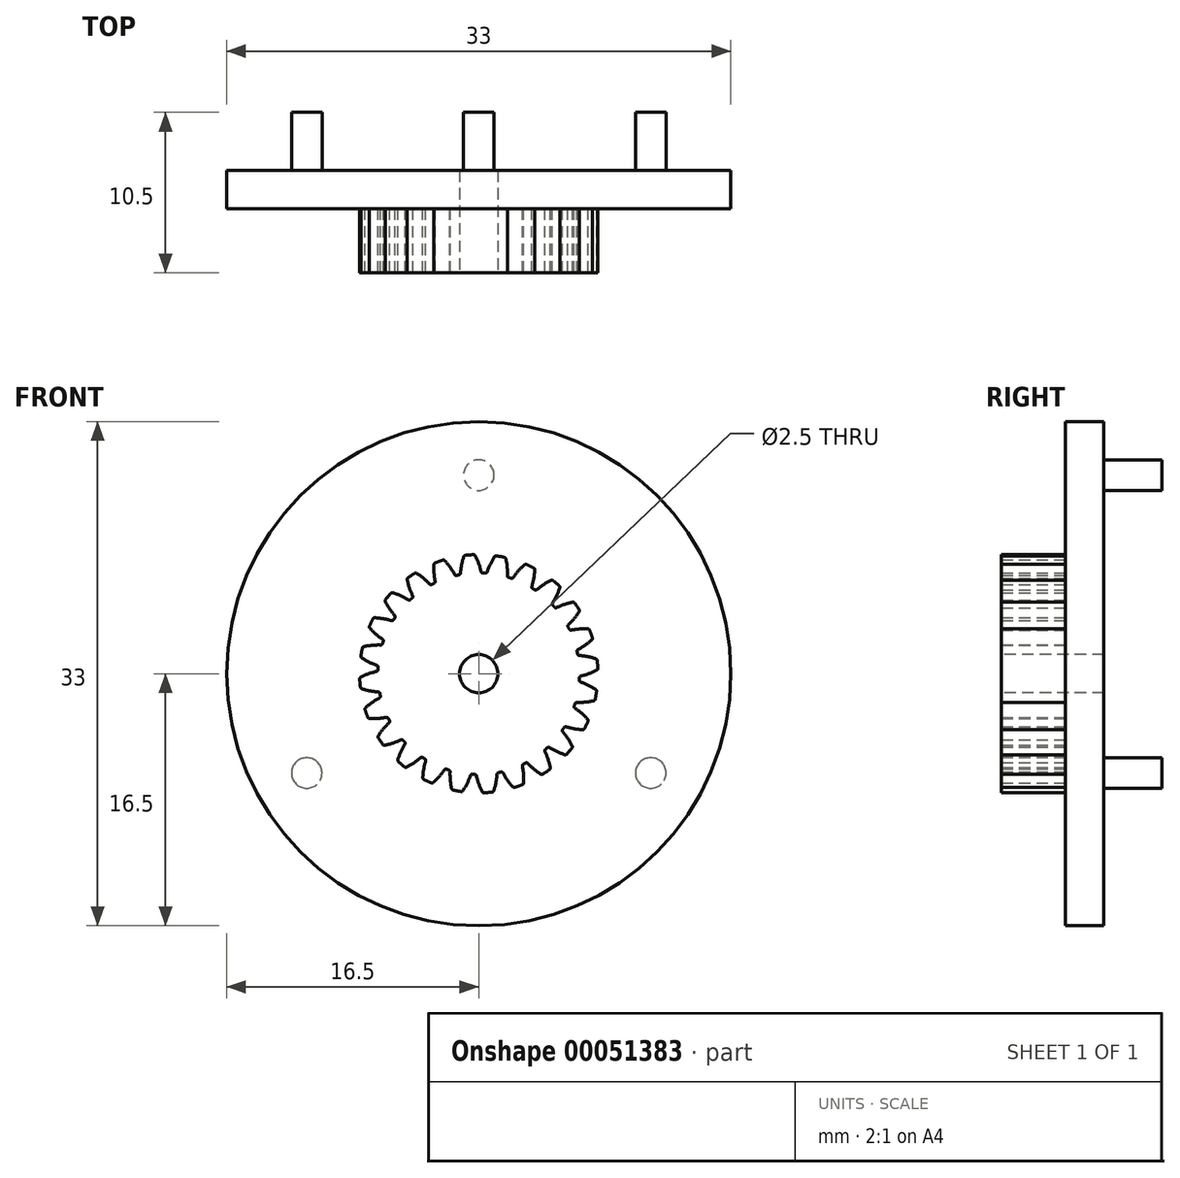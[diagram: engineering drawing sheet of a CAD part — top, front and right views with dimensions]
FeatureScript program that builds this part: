
annotation { "Feature Type Name" : "Feature", "Feature Type Description" : "" }
export const myFeature = defineFeature(function(context is Context, id is Id, definition is map)
    precondition{}
    {
        {
            var Q0;
            Q0=qCreatedBy(makeId("Front.planeOp"),FACE);
            var sketch = newSketch(context, id + "F0", { "sketchPlane" : qUnion([Q0])});
            skCircle(sketch, "E0", {"center": v(0, 0) * mm, "radius": 7.2 * mm, "construction": true});
            skCircle(sketch, "E1", {"center": v(0, 0) * mm, "radius": 6.6 * mm, "construction": true});
            skCircle(sketch, "E2", {"center": v(0, 0) * mm, "radius": 7.8 * mm, "construction": true});
            skLineSegment(sketch, "E3", {"start": v(0, 0) * mm, "end": v(0, 7.77) * mm, "construction": true});
            skPoint(sketch, "E4", {"position": v(0, 7.2) * mm});
            skLineSegment(sketch, "E5", {"start": v(0, 7.2) * mm, "end": v(-7.8, 7.2) * mm, "construction": true});
            skCircle(sketch, "E6.cCircle", {"center": v(0, 0) * mm, "radius": 7.77 * mm, "construction": true});
            skLineSegment(sketch, "E6.0", {"start": v(-0.61, 7.77) * mm, "end": v(0.61, 7.77) * mm, "construction": true});
            skLineSegment(sketch, "E6.1", {"start": v(0.61, 7.77) * mm, "end": v(1.82, 7.58) * mm, "construction": true});
            skLineSegment(sketch, "E6.2", {"start": v(1.82, 7.58) * mm, "end": v(2.98, 7.2) * mm, "construction": true});
            skLineSegment(sketch, "E6.3", {"start": v(2.98, 7.2) * mm, "end": v(4.07, 6.65) * mm, "construction": true});
            skLineSegment(sketch, "E6.4", {"start": v(4.07, 6.65) * mm, "end": v(5.06, 5.93) * mm, "construction": true});
            skLineSegment(sketch, "E6.5", {"start": v(5.06, 5.93) * mm, "end": v(5.93, 5.06) * mm, "construction": true});
            skLineSegment(sketch, "E6.6", {"start": v(5.93, 5.06) * mm, "end": v(6.65, 4.07) * mm, "construction": true});
            skLineSegment(sketch, "E6.7", {"start": v(6.65, 4.07) * mm, "end": v(7.2, 2.98) * mm, "construction": true});
            skLineSegment(sketch, "E6.8", {"start": v(7.2, 2.98) * mm, "end": v(7.58, 1.82) * mm, "construction": true});
            skLineSegment(sketch, "E6.9", {"start": v(7.58, 1.82) * mm, "end": v(7.77, 0.61) * mm, "construction": true});
            skLineSegment(sketch, "E6.10", {"start": v(7.77, 0.61) * mm, "end": v(7.77, -0.61) * mm, "construction": true});
            skLineSegment(sketch, "E6.11", {"start": v(7.77, -0.61) * mm, "end": v(7.58, -1.82) * mm, "construction": true});
            skLineSegment(sketch, "E6.12", {"start": v(7.58, -1.82) * mm, "end": v(7.2, -2.98) * mm, "construction": true});
            skLineSegment(sketch, "E6.13", {"start": v(7.2, -2.98) * mm, "end": v(6.65, -4.07) * mm, "construction": true});
            skLineSegment(sketch, "E6.14", {"start": v(6.65, -4.07) * mm, "end": v(5.93, -5.06) * mm, "construction": true});
            skLineSegment(sketch, "E6.15", {"start": v(5.93, -5.06) * mm, "end": v(5.06, -5.93) * mm, "construction": true});
            skLineSegment(sketch, "E6.16", {"start": v(5.06, -5.93) * mm, "end": v(4.07, -6.65) * mm, "construction": true});
            skLineSegment(sketch, "E6.17", {"start": v(4.07, -6.65) * mm, "end": v(2.98, -7.2) * mm, "construction": true});
            skLineSegment(sketch, "E6.18", {"start": v(2.98, -7.2) * mm, "end": v(1.82, -7.58) * mm, "construction": true});
            skLineSegment(sketch, "E6.19", {"start": v(1.82, -7.58) * mm, "end": v(0.61, -7.77) * mm, "construction": true});
            skLineSegment(sketch, "E6.20", {"start": v(0.61, -7.77) * mm, "end": v(-0.61, -7.77) * mm, "construction": true});
            skLineSegment(sketch, "E6.21", {"start": v(-0.61, -7.77) * mm, "end": v(-1.82, -7.58) * mm, "construction": true});
            skLineSegment(sketch, "E6.22", {"start": v(-1.82, -7.58) * mm, "end": v(-2.98, -7.2) * mm, "construction": true});
            skLineSegment(sketch, "E6.23", {"start": v(-2.98, -7.2) * mm, "end": v(-4.07, -6.65) * mm, "construction": true});
            skLineSegment(sketch, "E6.24", {"start": v(-4.07, -6.65) * mm, "end": v(-5.06, -5.93) * mm, "construction": true});
            skLineSegment(sketch, "E6.25", {"start": v(-5.06, -5.93) * mm, "end": v(-5.93, -5.06) * mm, "construction": true});
            skLineSegment(sketch, "E6.26", {"start": v(-5.93, -5.06) * mm, "end": v(-6.65, -4.07) * mm, "construction": true});
            skLineSegment(sketch, "E6.27", {"start": v(-6.65, -4.07) * mm, "end": v(-7.2, -2.98) * mm, "construction": true});
            skLineSegment(sketch, "E6.28", {"start": v(-7.2, -2.98) * mm, "end": v(-7.58, -1.82) * mm, "construction": true});
            skLineSegment(sketch, "E6.29", {"start": v(-7.58, -1.82) * mm, "end": v(-7.77, -0.61) * mm, "construction": true});
            skLineSegment(sketch, "E6.30", {"start": v(-7.77, -0.61) * mm, "end": v(-7.77, 0.61) * mm, "construction": true});
            skLineSegment(sketch, "E6.31", {"start": v(-7.77, 0.61) * mm, "end": v(-7.58, 1.82) * mm, "construction": true});
            skLineSegment(sketch, "E6.32", {"start": v(-7.58, 1.82) * mm, "end": v(-7.2, 2.98) * mm, "construction": true});
            skLineSegment(sketch, "E6.33", {"start": v(-7.2, 2.98) * mm, "end": v(-6.65, 4.07) * mm, "construction": true});
            skLineSegment(sketch, "E6.34", {"start": v(-6.65, 4.07) * mm, "end": v(-5.93, 5.06) * mm, "construction": true});
            skLineSegment(sketch, "E6.35", {"start": v(-5.93, 5.06) * mm, "end": v(-5.06, 5.93) * mm, "construction": true});
            skLineSegment(sketch, "E6.36", {"start": v(-5.06, 5.93) * mm, "end": v(-4.07, 6.65) * mm, "construction": true});
            skLineSegment(sketch, "E6.37", {"start": v(-4.07, 6.65) * mm, "end": v(-2.98, 7.2) * mm, "construction": true});
            skLineSegment(sketch, "E6.38", {"start": v(-2.98, 7.2) * mm, "end": v(-1.82, 7.58) * mm, "construction": true});
            skLineSegment(sketch, "E6.39", {"start": v(-1.82, 7.58) * mm, "end": v(-0.61, 7.77) * mm, "construction": true});
            skPoint(sketch, "E6.0.midPoint", {"position": v(0, 7.77) * mm});
            skLineSegment(sketch, "E7.0", {"start": v(0, 7.77) * mm, "end": v(1.22, 7.68) * mm, "construction": true});
            skLineSegment(sketch, "E7.1", {"start": v(1.22, 7.68) * mm, "end": v(2.4, 7.4) * mm, "construction": true});
            skLineSegment(sketch, "E7.2", {"start": v(2.4, 7.4) * mm, "end": v(3.53, 6.93) * mm, "construction": true});
            skLineSegment(sketch, "E7.3", {"start": v(3.53, 6.93) * mm, "end": v(4.57, 6.29) * mm, "construction": true});
            skLineSegment(sketch, "E7.4", {"start": v(4.57, 6.29) * mm, "end": v(5.5, 5.5) * mm, "construction": true});
            skLineSegment(sketch, "E7.5", {"start": v(5.5, 5.5) * mm, "end": v(6.29, 4.57) * mm, "construction": true});
            skLineSegment(sketch, "E7.6", {"start": v(6.29, 4.57) * mm, "end": v(6.93, 3.53) * mm, "construction": true});
            skLineSegment(sketch, "E7.7", {"start": v(6.93, 3.53) * mm, "end": v(7.4, 2.4) * mm, "construction": true});
            skLineSegment(sketch, "E7.8", {"start": v(7.4, 2.4) * mm, "end": v(7.68, 1.22) * mm, "construction": true});
            skLineSegment(sketch, "E7.9", {"start": v(7.68, 1.22) * mm, "end": v(7.77, 0) * mm, "construction": true});
            skLineSegment(sketch, "E7.10", {"start": v(7.77, 0) * mm, "end": v(7.68, -1.22) * mm, "construction": true});
            skLineSegment(sketch, "E7.11", {"start": v(7.68, -1.22) * mm, "end": v(7.4, -2.4) * mm, "construction": true});
            skLineSegment(sketch, "E7.12", {"start": v(7.4, -2.4) * mm, "end": v(6.93, -3.53) * mm, "construction": true});
            skLineSegment(sketch, "E7.13", {"start": v(6.93, -3.53) * mm, "end": v(6.29, -4.57) * mm, "construction": true});
            skLineSegment(sketch, "E7.14", {"start": v(6.29, -4.57) * mm, "end": v(5.5, -5.5) * mm, "construction": true});
            skLineSegment(sketch, "E7.15", {"start": v(5.5, -5.5) * mm, "end": v(4.57, -6.29) * mm, "construction": true});
            skLineSegment(sketch, "E7.16", {"start": v(4.57, -6.29) * mm, "end": v(3.53, -6.93) * mm, "construction": true});
            skLineSegment(sketch, "E7.17", {"start": v(3.53, -6.93) * mm, "end": v(2.4, -7.4) * mm, "construction": true});
            skLineSegment(sketch, "E7.18", {"start": v(2.4, -7.4) * mm, "end": v(1.22, -7.68) * mm, "construction": true});
            skLineSegment(sketch, "E7.19", {"start": v(1.22, -7.68) * mm, "end": v(0, -7.77) * mm, "construction": true});
            skLineSegment(sketch, "E7.20", {"start": v(0, -7.77) * mm, "end": v(-1.22, -7.68) * mm, "construction": true});
            skLineSegment(sketch, "E7.21", {"start": v(-1.22, -7.68) * mm, "end": v(-2.4, -7.4) * mm, "construction": true});
            skLineSegment(sketch, "E7.22", {"start": v(-2.4, -7.4) * mm, "end": v(-3.53, -6.93) * mm, "construction": true});
            skLineSegment(sketch, "E7.23", {"start": v(-3.53, -6.93) * mm, "end": v(-4.57, -6.29) * mm, "construction": true});
            skLineSegment(sketch, "E7.24", {"start": v(-4.57, -6.29) * mm, "end": v(-5.5, -5.5) * mm, "construction": true});
            skLineSegment(sketch, "E7.25", {"start": v(-5.5, -5.5) * mm, "end": v(-6.29, -4.57) * mm, "construction": true});
            skLineSegment(sketch, "E7.26", {"start": v(-6.29, -4.57) * mm, "end": v(-6.93, -3.53) * mm, "construction": true});
            skLineSegment(sketch, "E7.27", {"start": v(-6.93, -3.53) * mm, "end": v(-7.4, -2.4) * mm, "construction": true});
            skLineSegment(sketch, "E7.28", {"start": v(-7.4, -2.4) * mm, "end": v(-7.68, -1.22) * mm, "construction": true});
            skLineSegment(sketch, "E7.29", {"start": v(-7.68, -1.22) * mm, "end": v(-7.77, 0) * mm, "construction": true});
            skLineSegment(sketch, "E7.30", {"start": v(-7.77, 0) * mm, "end": v(-7.68, 1.22) * mm, "construction": true});
            skLineSegment(sketch, "E7.31", {"start": v(-7.68, 1.22) * mm, "end": v(-7.4, 2.4) * mm, "construction": true});
            skLineSegment(sketch, "E7.32", {"start": v(-7.4, 2.4) * mm, "end": v(-6.93, 3.53) * mm, "construction": true});
            skLineSegment(sketch, "E7.33", {"start": v(-6.93, 3.53) * mm, "end": v(-6.29, 4.57) * mm, "construction": true});
            skLineSegment(sketch, "E7.34", {"start": v(-6.29, 4.57) * mm, "end": v(-5.5, 5.5) * mm, "construction": true});
            skLineSegment(sketch, "E7.35", {"start": v(-5.5, 5.5) * mm, "end": v(-4.57, 6.29) * mm, "construction": true});
            skLineSegment(sketch, "E7.36", {"start": v(-4.57, 6.29) * mm, "end": v(-3.53, 6.93) * mm, "construction": true});
            skLineSegment(sketch, "E7.37", {"start": v(-3.53, 6.93) * mm, "end": v(-2.4, 7.4) * mm, "construction": true});
            skLineSegment(sketch, "E7.38", {"start": v(-2.4, 7.4) * mm, "end": v(-1.22, 7.68) * mm, "construction": true});
            skLineSegment(sketch, "E7.39", {"start": v(-1.22, 7.68) * mm, "end": v(0, 7.77) * mm, "construction": true});
            skLineSegment(sketch, "E8", {"start": v(0, 0) * mm, "end": v(-0.61, 7.77) * mm, "construction": true});
            skLineSegment(sketch, "E9", {"start": v(0, 7.2) * mm, "end": v(-7.35, 4.52) * mm, "construction": true});
            skCircle(sketch, "E10", {"center": v(0, 7.2) * mm, "radius": 4.32 * mm, "construction": true});
            skPoint(sketch, "E11", {"position": v(-4.06, 5.72) * mm});
            skCircle(sketch, "E12", {"center": v(-4.06, 5.72) * mm, "radius": 4.32 * mm, "construction": true});
            skArc(sketch, "E13", {"start": v(-0.23, 7.73) * mm, "mid": v(0, 7.22) * mm, "end": v(0.15, 6.69) * mm});
            skArc(sketch, "E14.MirrorCS", {"start": v(-0.98, 7.67) * mm, "mid": v(-1.12, 7.13) * mm, "end": v(-1.2, 6.58) * mm});
            skArc(sketch, "E15", {"start": v(-0.88, 7.75) * mm, "mid": v(-0.61, 7.78) * mm, "end": v(-0.34, 7.8) * mm});
            skArc(sketch, "E16", {"start": v(-1.3, 6.47) * mm, "mid": v(0.52, -6.58) * mm, "end": v(0.26, 6.6) * mm});
            skPoint(sketch, "E17.visualSharp", {"position": v(-1.2, 6.49) * mm});
            skArc(sketch, "E17.filletArc", {"start": v(-1.3, 6.47) * mm, "mid": v(-1.23, 6.51) * mm, "end": v(-1.2, 6.58) * mm});
            skPoint(sketch, "E18.visualSharp", {"position": v(0.17, 6.6) * mm});
            skArc(sketch, "E18.filletArc", {"start": v(0.15, 6.69) * mm, "mid": v(0.2, 6.62) * mm, "end": v(0.26, 6.6) * mm});
            skPoint(sketch, "E19.visualSharp", {"position": v(-0.95, 7.74) * mm});
            skArc(sketch, "E19.filletArc", {"start": v(-0.88, 7.75) * mm, "mid": v(-0.94, 7.72) * mm, "end": v(-0.98, 7.67) * mm});
            skPoint(sketch, "E20.visualSharp", {"position": v(-0.27, 7.8) * mm});
            skArc(sketch, "E20.filletArc", {"start": v(-0.23, 7.73) * mm, "mid": v(-0.28, 7.78) * mm, "end": v(-0.34, 7.8) * mm});
            skLineSegment(sketch, "E21", {"start": v(0, 0) * mm, "end": v(-1.62, 8.11) * mm, "construction": true});
            skPoint(sketch, "E22.1.0", {"position": v(-1.54, 6.42) * mm});
            skPoint(sketch, "E22.1.1", {"position": v(-1.86, 6.95) * mm});
            skArc(sketch, "E22.1.2", {"start": v(-2.23, 7.4) * mm, "mid": v(-1.88, 6.97) * mm, "end": v(-1.58, 6.5) * mm});
            skArc(sketch, "E22.1.3", {"start": v(-2.85, 7.26) * mm, "mid": v(-2.6, 7.35) * mm, "end": v(-2.35, 7.44) * mm});
            skPoint(sketch, "E22.1.4", {"position": v(-2.28, 7.46) * mm});
            skPoint(sketch, "E22.1.5", {"position": v(-2.84, 5.96) * mm});
            skArc(sketch, "E22.1.6", {"start": v(-2.93, 7.15) * mm, "mid": v(-2.93, 6.6) * mm, "end": v(-2.86, 6.05) * mm});
            skPoint(sketch, "E22.1.7", {"position": v(-2.92, 7.23) * mm});
            skArc(sketch, "E22.1.8", {"start": v(-1.58, 6.5) * mm, "mid": v(-1.53, 6.45) * mm, "end": v(-1.45, 6.44) * mm});
            skArc(sketch, "E22.1.9", {"start": v(-2.85, 7.26) * mm, "mid": v(-2.9, 7.22) * mm, "end": v(-2.93, 7.15) * mm});
            skArc(sketch, "E22.1.10", {"start": v(-2.92, 5.92) * mm, "mid": v(-2.87, 5.97) * mm, "end": v(-2.86, 6.05) * mm});
            skArc(sketch, "E22.1.11", {"start": v(-2.23, 7.4) * mm, "mid": v(-2.28, 7.44) * mm, "end": v(-2.35, 7.44) * mm});
            skPoint(sketch, "E22.2.0", {"position": v(-3.15, 5.8) * mm});
            skPoint(sketch, "E22.2.1", {"position": v(-3.6, 6.24) * mm});
            skArc(sketch, "E22.2.2", {"start": v(-4.07, 6.58) * mm, "mid": v(-3.62, 6.25) * mm, "end": v(-3.21, 5.87) * mm});
            skArc(sketch, "E22.2.3", {"start": v(-4.64, 6.27) * mm, "mid": v(-4.42, 6.43) * mm, "end": v(-4.2, 6.58) * mm});
            skPoint(sketch, "E22.2.4", {"position": v(-4.13, 6.62) * mm});
            skPoint(sketch, "E22.2.5", {"position": v(-4.28, 5.02) * mm});
            skArc(sketch, "E22.2.6", {"start": v(-4.68, 6.15) * mm, "mid": v(-4.54, 5.62) * mm, "end": v(-4.33, 5.1) * mm});
            skPoint(sketch, "E22.2.7", {"position": v(-4.7, 6.23) * mm});
            skArc(sketch, "E22.2.8", {"start": v(-3.21, 5.87) * mm, "mid": v(-3.15, 5.83) * mm, "end": v(-3.07, 5.84) * mm});
            skArc(sketch, "E22.2.9", {"start": v(-4.64, 6.27) * mm, "mid": v(-4.68, 6.22) * mm, "end": v(-4.68, 6.15) * mm});
            skArc(sketch, "E22.2.10", {"start": v(-4.35, 4.96) * mm, "mid": v(-4.32, 5.03) * mm, "end": v(-4.33, 5.1) * mm});
            skArc(sketch, "E22.2.11", {"start": v(-4.07, 6.58) * mm, "mid": v(-4.13, 6.6) * mm, "end": v(-4.2, 6.58) * mm});
            skPoint(sketch, "E22.3.0", {"position": v(-4.54, 4.79) * mm});
            skPoint(sketch, "E22.3.1", {"position": v(-5.1, 5.1) * mm});
            skArc(sketch, "E22.3.2", {"start": v(-5.63, 5.3) * mm, "mid": v(-5.11, 5.1) * mm, "end": v(-4.62, 4.84) * mm});
            skArc(sketch, "E22.3.3", {"start": v(-6.1, 4.86) * mm, "mid": v(-5.93, 5.07) * mm, "end": v(-5.75, 5.27) * mm});
            skPoint(sketch, "E22.3.4", {"position": v(-5.7, 5.32) * mm});
            skPoint(sketch, "E22.3.5", {"position": v(-5.44, 3.74) * mm});
            skArc(sketch, "E22.3.6", {"start": v(-6.12, 4.73) * mm, "mid": v(-5.84, 4.25) * mm, "end": v(-5.5, 3.8) * mm});
            skPoint(sketch, "E22.3.7", {"position": v(-6.15, 4.8) * mm});
            skArc(sketch, "E22.3.8", {"start": v(-4.62, 4.84) * mm, "mid": v(-4.55, 4.82) * mm, "end": v(-4.48, 4.85) * mm});
            skArc(sketch, "E22.3.9", {"start": v(-6.1, 4.86) * mm, "mid": v(-6.13, 4.8) * mm, "end": v(-6.12, 4.73) * mm});
            skArc(sketch, "E22.3.10", {"start": v(-5.5, 3.66) * mm, "mid": v(-5.47, 3.74) * mm, "end": v(-5.5, 3.8) * mm});
            skArc(sketch, "E22.3.11", {"start": v(-5.63, 5.3) * mm, "mid": v(-5.7, 5.3) * mm, "end": v(-5.75, 5.27) * mm});
            skPoint(sketch, "E22.4.0", {"position": v(-5.63, 3.45) * mm});
            skPoint(sketch, "E22.4.1", {"position": v(-6.24, 3.6) * mm});
            skArc(sketch, "E22.4.2", {"start": v(-6.8, 3.66) * mm, "mid": v(-6.26, 3.6) * mm, "end": v(-5.72, 3.47) * mm});
            skArc(sketch, "E22.4.3", {"start": v(-7.15, 3.11) * mm, "mid": v(-7.04, 3.36) * mm, "end": v(-6.92, 3.6) * mm});
            skPoint(sketch, "E22.4.4", {"position": v(-6.89, 3.66) * mm});
            skPoint(sketch, "E22.4.5", {"position": v(-6.22, 2.2) * mm});
            skArc(sketch, "E22.4.6", {"start": v(-7.13, 2.99) * mm, "mid": v(-6.74, 2.6) * mm, "end": v(-6.3, 2.26) * mm});
            skPoint(sketch, "E22.4.7", {"position": v(-7.18, 3.04) * mm});
            skArc(sketch, "E22.4.8", {"start": v(-5.72, 3.47) * mm, "mid": v(-5.64, 3.48) * mm, "end": v(-5.58, 3.53) * mm});
            skArc(sketch, "E22.4.9", {"start": v(-7.15, 3.11) * mm, "mid": v(-7.16, 3.05) * mm, "end": v(-7.13, 2.99) * mm});
            skArc(sketch, "E22.4.10", {"start": v(-6.25, 2.12) * mm, "mid": v(-6.25, 2.2) * mm, "end": v(-6.3, 2.26) * mm});
            skArc(sketch, "E22.4.11", {"start": v(-6.8, 3.66) * mm, "mid": v(-6.87, 3.65) * mm, "end": v(-6.92, 3.6) * mm});
            skPoint(sketch, "E22.5.0", {"position": v(-6.33, 1.87) * mm});
            skPoint(sketch, "E22.5.1", {"position": v(-6.95, 1.86) * mm});
            skArc(sketch, "E22.5.2", {"start": v(-7.53, 1.77) * mm, "mid": v(-6.98, 1.86) * mm, "end": v(-6.42, 1.88) * mm});
            skArc(sketch, "E22.5.3", {"start": v(-7.71, 1.16) * mm, "mid": v(-7.67, 1.42) * mm, "end": v(-7.62, 1.68) * mm});
            skPoint(sketch, "E22.5.4", {"position": v(-7.6, 1.76) * mm});
            skPoint(sketch, "E22.5.5", {"position": v(-6.58, 0.52) * mm});
            skArc(sketch, "E22.5.6", {"start": v(-7.66, 1.04) * mm, "mid": v(-7.18, 0.76) * mm, "end": v(-6.67, 0.55) * mm});
            skPoint(sketch, "E22.5.7", {"position": v(-7.72, 1.08) * mm});
            skArc(sketch, "E22.5.8", {"start": v(-6.42, 1.88) * mm, "mid": v(-6.35, 1.9) * mm, "end": v(-6.3, 1.96) * mm});
            skArc(sketch, "E22.5.9", {"start": v(-7.71, 1.16) * mm, "mid": v(-7.7, 1.1) * mm, "end": v(-7.66, 1.04) * mm});
            skArc(sketch, "E22.5.10", {"start": v(-6.59, 0.43) * mm, "mid": v(-6.6, 0.5) * mm, "end": v(-6.67, 0.55) * mm});
            skArc(sketch, "E22.5.11", {"start": v(-7.53, 1.77) * mm, "mid": v(-7.58, 1.74) * mm, "end": v(-7.62, 1.68) * mm});
            skPoint(sketch, "E22.6.0", {"position": v(-6.6, 0.17) * mm});
            skPoint(sketch, "E22.6.1", {"position": v(-7.2, 0) * mm});
            skArc(sketch, "E22.6.2", {"start": v(-7.73, -0.23) * mm, "mid": v(-7.22, 0) * mm, "end": v(-6.69, 0.15) * mm});
            skArc(sketch, "E22.6.3", {"start": v(-7.75, -0.88) * mm, "mid": v(-7.78, -0.61) * mm, "end": v(-7.8, -0.34) * mm});
            skPoint(sketch, "E22.6.4", {"position": v(-7.8, -0.27) * mm});
            skPoint(sketch, "E22.6.5", {"position": v(-6.49, -1.2) * mm});
            skArc(sketch, "E22.6.6", {"start": v(-7.67, -0.98) * mm, "mid": v(-7.13, -1.12) * mm, "end": v(-6.58, -1.2) * mm});
            skPoint(sketch, "E22.6.7", {"position": v(-7.74, -0.95) * mm});
            skArc(sketch, "E22.6.8", {"start": v(-6.69, 0.15) * mm, "mid": v(-6.62, 0.2) * mm, "end": v(-6.6, 0.26) * mm});
            skArc(sketch, "E22.6.9", {"start": v(-7.75, -0.88) * mm, "mid": v(-7.72, -0.94) * mm, "end": v(-7.67, -0.98) * mm});
            skArc(sketch, "E22.6.10", {"start": v(-6.47, -1.3) * mm, "mid": v(-6.51, -1.23) * mm, "end": v(-6.58, -1.2) * mm});
            skArc(sketch, "E22.6.11", {"start": v(-7.73, -0.23) * mm, "mid": v(-7.78, -0.28) * mm, "end": v(-7.8, -0.34) * mm});
            skPoint(sketch, "E22.7.0", {"position": v(-6.42, -1.54) * mm});
            skPoint(sketch, "E22.7.1", {"position": v(-6.95, -1.86) * mm});
            skArc(sketch, "E22.7.2", {"start": v(-7.4, -2.23) * mm, "mid": v(-6.97, -1.88) * mm, "end": v(-6.5, -1.58) * mm});
            skArc(sketch, "E22.7.3", {"start": v(-7.26, -2.85) * mm, "mid": v(-7.35, -2.6) * mm, "end": v(-7.44, -2.35) * mm});
            skPoint(sketch, "E22.7.4", {"position": v(-7.46, -2.28) * mm});
            skPoint(sketch, "E22.7.5", {"position": v(-5.96, -2.84) * mm});
            skArc(sketch, "E22.7.6", {"start": v(-7.15, -2.93) * mm, "mid": v(-6.6, -2.93) * mm, "end": v(-6.05, -2.86) * mm});
            skPoint(sketch, "E22.7.7", {"position": v(-7.23, -2.92) * mm});
            skArc(sketch, "E22.7.8", {"start": v(-6.5, -1.58) * mm, "mid": v(-6.45, -1.53) * mm, "end": v(-6.44, -1.45) * mm});
            skArc(sketch, "E22.7.9", {"start": v(-7.26, -2.85) * mm, "mid": v(-7.22, -2.9) * mm, "end": v(-7.15, -2.93) * mm});
            skArc(sketch, "E22.7.10", {"start": v(-5.92, -2.92) * mm, "mid": v(-5.97, -2.87) * mm, "end": v(-6.05, -2.86) * mm});
            skArc(sketch, "E22.7.11", {"start": v(-7.4, -2.23) * mm, "mid": v(-7.44, -2.28) * mm, "end": v(-7.44, -2.35) * mm});
            skPoint(sketch, "E22.8.0", {"position": v(-5.8, -3.15) * mm});
            skPoint(sketch, "E22.8.1", {"position": v(-6.24, -3.6) * mm});
            skArc(sketch, "E22.8.2", {"start": v(-6.58, -4.07) * mm, "mid": v(-6.25, -3.62) * mm, "end": v(-5.87, -3.21) * mm});
            skArc(sketch, "E22.8.3", {"start": v(-6.27, -4.64) * mm, "mid": v(-6.43, -4.42) * mm, "end": v(-6.58, -4.2) * mm});
            skPoint(sketch, "E22.8.4", {"position": v(-6.62, -4.13) * mm});
            skPoint(sketch, "E22.8.5", {"position": v(-5.02, -4.28) * mm});
            skArc(sketch, "E22.8.6", {"start": v(-6.15, -4.68) * mm, "mid": v(-5.62, -4.54) * mm, "end": v(-5.1, -4.33) * mm});
            skPoint(sketch, "E22.8.7", {"position": v(-6.23, -4.7) * mm});
            skArc(sketch, "E22.8.8", {"start": v(-5.87, -3.21) * mm, "mid": v(-5.83, -3.15) * mm, "end": v(-5.84, -3.07) * mm});
            skArc(sketch, "E22.8.9", {"start": v(-6.27, -4.64) * mm, "mid": v(-6.22, -4.68) * mm, "end": v(-6.15, -4.68) * mm});
            skArc(sketch, "E22.8.10", {"start": v(-4.96, -4.35) * mm, "mid": v(-5.03, -4.32) * mm, "end": v(-5.1, -4.33) * mm});
            skArc(sketch, "E22.8.11", {"start": v(-6.58, -4.07) * mm, "mid": v(-6.6, -4.13) * mm, "end": v(-6.58, -4.2) * mm});
            skPoint(sketch, "E22.9.0", {"position": v(-4.79, -4.54) * mm});
            skPoint(sketch, "E22.9.1", {"position": v(-5.1, -5.1) * mm});
            skArc(sketch, "E22.9.2", {"start": v(-5.3, -5.63) * mm, "mid": v(-5.1, -5.11) * mm, "end": v(-4.84, -4.62) * mm});
            skArc(sketch, "E22.9.3", {"start": v(-4.86, -6.1) * mm, "mid": v(-5.07, -5.93) * mm, "end": v(-5.27, -5.75) * mm});
            skPoint(sketch, "E22.9.4", {"position": v(-5.32, -5.7) * mm});
            skPoint(sketch, "E22.9.5", {"position": v(-3.74, -5.44) * mm});
            skArc(sketch, "E22.9.6", {"start": v(-4.73, -6.12) * mm, "mid": v(-4.25, -5.84) * mm, "end": v(-3.8, -5.5) * mm});
            skPoint(sketch, "E22.9.7", {"position": v(-4.8, -6.15) * mm});
            skArc(sketch, "E22.9.8", {"start": v(-4.84, -4.62) * mm, "mid": v(-4.82, -4.55) * mm, "end": v(-4.85, -4.48) * mm});
            skArc(sketch, "E22.9.9", {"start": v(-4.86, -6.1) * mm, "mid": v(-4.8, -6.13) * mm, "end": v(-4.73, -6.12) * mm});
            skArc(sketch, "E22.9.10", {"start": v(-3.66, -5.5) * mm, "mid": v(-3.74, -5.47) * mm, "end": v(-3.8, -5.5) * mm});
            skArc(sketch, "E22.9.11", {"start": v(-5.3, -5.63) * mm, "mid": v(-5.3, -5.7) * mm, "end": v(-5.27, -5.75) * mm});
            skPoint(sketch, "E22.10.0", {"position": v(-3.45, -5.63) * mm});
            skPoint(sketch, "E22.10.1", {"position": v(-3.6, -6.24) * mm});
            skArc(sketch, "E22.10.2", {"start": v(-3.66, -6.8) * mm, "mid": v(-3.6, -6.26) * mm, "end": v(-3.47, -5.72) * mm});
            skArc(sketch, "E22.10.3", {"start": v(-3.11, -7.15) * mm, "mid": v(-3.36, -7.04) * mm, "end": v(-3.6, -6.92) * mm});
            skPoint(sketch, "E22.10.4", {"position": v(-3.66, -6.89) * mm});
            skPoint(sketch, "E22.10.5", {"position": v(-2.2, -6.22) * mm});
            skArc(sketch, "E22.10.6", {"start": v(-2.99, -7.13) * mm, "mid": v(-2.6, -6.74) * mm, "end": v(-2.26, -6.3) * mm});
            skPoint(sketch, "E22.10.7", {"position": v(-3.04, -7.18) * mm});
            skArc(sketch, "E22.10.8", {"start": v(-3.47, -5.72) * mm, "mid": v(-3.48, -5.64) * mm, "end": v(-3.53, -5.58) * mm});
            skArc(sketch, "E22.10.9", {"start": v(-3.11, -7.15) * mm, "mid": v(-3.05, -7.16) * mm, "end": v(-2.99, -7.13) * mm});
            skArc(sketch, "E22.10.10", {"start": v(-2.12, -6.25) * mm, "mid": v(-2.2, -6.25) * mm, "end": v(-2.26, -6.3) * mm});
            skArc(sketch, "E22.10.11", {"start": v(-3.66, -6.8) * mm, "mid": v(-3.65, -6.87) * mm, "end": v(-3.6, -6.92) * mm});
            skPoint(sketch, "E22.11.0", {"position": v(-1.87, -6.33) * mm});
            skPoint(sketch, "E22.11.1", {"position": v(-1.86, -6.95) * mm});
            skArc(sketch, "E22.11.2", {"start": v(-1.77, -7.53) * mm, "mid": v(-1.86, -6.98) * mm, "end": v(-1.88, -6.42) * mm});
            skArc(sketch, "E22.11.3", {"start": v(-1.16, -7.71) * mm, "mid": v(-1.42, -7.67) * mm, "end": v(-1.68, -7.62) * mm});
            skPoint(sketch, "E22.11.4", {"position": v(-1.76, -7.6) * mm});
            skPoint(sketch, "E22.11.5", {"position": v(-0.52, -6.58) * mm});
            skArc(sketch, "E22.11.6", {"start": v(-1.04, -7.66) * mm, "mid": v(-0.76, -7.18) * mm, "end": v(-0.55, -6.67) * mm});
            skPoint(sketch, "E22.11.7", {"position": v(-1.08, -7.72) * mm});
            skArc(sketch, "E22.11.8", {"start": v(-1.88, -6.42) * mm, "mid": v(-1.9, -6.35) * mm, "end": v(-1.96, -6.3) * mm});
            skArc(sketch, "E22.11.9", {"start": v(-1.16, -7.71) * mm, "mid": v(-1.1, -7.7) * mm, "end": v(-1.04, -7.66) * mm});
            skArc(sketch, "E22.11.10", {"start": v(-0.43, -6.59) * mm, "mid": v(-0.5, -6.6) * mm, "end": v(-0.55, -6.67) * mm});
            skArc(sketch, "E22.11.11", {"start": v(-1.77, -7.53) * mm, "mid": v(-1.74, -7.58) * mm, "end": v(-1.68, -7.62) * mm});
            skPoint(sketch, "E22.12.0", {"position": v(-0.17, -6.6) * mm});
            skPoint(sketch, "E22.12.1", {"position": v(0, -7.2) * mm});
            skArc(sketch, "E22.12.2", {"start": v(0.23, -7.73) * mm, "mid": v(0, -7.22) * mm, "end": v(-0.15, -6.69) * mm});
            skArc(sketch, "E22.12.3", {"start": v(0.88, -7.75) * mm, "mid": v(0.61, -7.78) * mm, "end": v(0.34, -7.8) * mm});
            skPoint(sketch, "E22.12.4", {"position": v(0.27, -7.8) * mm});
            skPoint(sketch, "E22.12.5", {"position": v(1.2, -6.49) * mm});
            skArc(sketch, "E22.12.6", {"start": v(0.98, -7.67) * mm, "mid": v(1.12, -7.13) * mm, "end": v(1.2, -6.58) * mm});
            skPoint(sketch, "E22.12.7", {"position": v(0.95, -7.74) * mm});
            skArc(sketch, "E22.12.8", {"start": v(-0.15, -6.69) * mm, "mid": v(-0.2, -6.62) * mm, "end": v(-0.26, -6.6) * mm});
            skArc(sketch, "E22.12.9", {"start": v(0.88, -7.75) * mm, "mid": v(0.94, -7.72) * mm, "end": v(0.98, -7.67) * mm});
            skArc(sketch, "E22.12.10", {"start": v(1.3, -6.47) * mm, "mid": v(1.23, -6.51) * mm, "end": v(1.2, -6.58) * mm});
            skArc(sketch, "E22.12.11", {"start": v(0.23, -7.73) * mm, "mid": v(0.28, -7.78) * mm, "end": v(0.34, -7.8) * mm});
            skPoint(sketch, "E22.13.0", {"position": v(1.54, -6.42) * mm});
            skPoint(sketch, "E22.13.1", {"position": v(1.86, -6.95) * mm});
            skArc(sketch, "E22.13.2", {"start": v(2.23, -7.4) * mm, "mid": v(1.88, -6.97) * mm, "end": v(1.58, -6.5) * mm});
            skArc(sketch, "E22.13.3", {"start": v(2.85, -7.26) * mm, "mid": v(2.6, -7.35) * mm, "end": v(2.35, -7.44) * mm});
            skPoint(sketch, "E22.13.4", {"position": v(2.28, -7.46) * mm});
            skPoint(sketch, "E22.13.5", {"position": v(2.84, -5.96) * mm});
            skArc(sketch, "E22.13.6", {"start": v(2.93, -7.15) * mm, "mid": v(2.93, -6.6) * mm, "end": v(2.86, -6.05) * mm});
            skPoint(sketch, "E22.13.7", {"position": v(2.92, -7.23) * mm});
            skArc(sketch, "E22.13.8", {"start": v(1.58, -6.5) * mm, "mid": v(1.53, -6.45) * mm, "end": v(1.45, -6.44) * mm});
            skArc(sketch, "E22.13.9", {"start": v(2.85, -7.26) * mm, "mid": v(2.9, -7.22) * mm, "end": v(2.93, -7.15) * mm});
            skArc(sketch, "E22.13.10", {"start": v(2.92, -5.92) * mm, "mid": v(2.87, -5.97) * mm, "end": v(2.86, -6.05) * mm});
            skArc(sketch, "E22.13.11", {"start": v(2.23, -7.4) * mm, "mid": v(2.28, -7.44) * mm, "end": v(2.35, -7.44) * mm});
            skPoint(sketch, "E22.14.0", {"position": v(3.15, -5.8) * mm});
            skPoint(sketch, "E22.14.1", {"position": v(3.6, -6.24) * mm});
            skArc(sketch, "E22.14.2", {"start": v(4.07, -6.58) * mm, "mid": v(3.62, -6.25) * mm, "end": v(3.21, -5.87) * mm});
            skArc(sketch, "E22.14.3", {"start": v(4.64, -6.27) * mm, "mid": v(4.42, -6.43) * mm, "end": v(4.2, -6.58) * mm});
            skPoint(sketch, "E22.14.4", {"position": v(4.13, -6.62) * mm});
            skPoint(sketch, "E22.14.5", {"position": v(4.28, -5.02) * mm});
            skArc(sketch, "E22.14.6", {"start": v(4.68, -6.15) * mm, "mid": v(4.54, -5.62) * mm, "end": v(4.33, -5.1) * mm});
            skPoint(sketch, "E22.14.7", {"position": v(4.7, -6.23) * mm});
            skArc(sketch, "E22.14.8", {"start": v(3.21, -5.87) * mm, "mid": v(3.15, -5.83) * mm, "end": v(3.07, -5.84) * mm});
            skArc(sketch, "E22.14.9", {"start": v(4.64, -6.27) * mm, "mid": v(4.68, -6.22) * mm, "end": v(4.68, -6.15) * mm});
            skArc(sketch, "E22.14.10", {"start": v(4.35, -4.96) * mm, "mid": v(4.32, -5.03) * mm, "end": v(4.33, -5.1) * mm});
            skArc(sketch, "E22.14.11", {"start": v(4.07, -6.58) * mm, "mid": v(4.13, -6.6) * mm, "end": v(4.2, -6.58) * mm});
            skPoint(sketch, "E22.15.0", {"position": v(4.54, -4.79) * mm});
            skPoint(sketch, "E22.15.1", {"position": v(5.1, -5.1) * mm});
            skArc(sketch, "E22.15.2", {"start": v(5.63, -5.3) * mm, "mid": v(5.11, -5.1) * mm, "end": v(4.62, -4.84) * mm});
            skArc(sketch, "E22.15.3", {"start": v(6.1, -4.86) * mm, "mid": v(5.93, -5.07) * mm, "end": v(5.75, -5.27) * mm});
            skPoint(sketch, "E22.15.4", {"position": v(5.7, -5.32) * mm});
            skPoint(sketch, "E22.15.5", {"position": v(5.44, -3.74) * mm});
            skArc(sketch, "E22.15.6", {"start": v(6.12, -4.73) * mm, "mid": v(5.84, -4.25) * mm, "end": v(5.5, -3.8) * mm});
            skPoint(sketch, "E22.15.7", {"position": v(6.15, -4.8) * mm});
            skArc(sketch, "E22.15.8", {"start": v(4.62, -4.84) * mm, "mid": v(4.55, -4.82) * mm, "end": v(4.48, -4.85) * mm});
            skArc(sketch, "E22.15.9", {"start": v(6.1, -4.86) * mm, "mid": v(6.13, -4.8) * mm, "end": v(6.12, -4.73) * mm});
            skArc(sketch, "E22.15.10", {"start": v(5.5, -3.66) * mm, "mid": v(5.47, -3.74) * mm, "end": v(5.5, -3.8) * mm});
            skArc(sketch, "E22.15.11", {"start": v(5.63, -5.3) * mm, "mid": v(5.7, -5.3) * mm, "end": v(5.75, -5.27) * mm});
            skPoint(sketch, "E22.16.0", {"position": v(5.63, -3.45) * mm});
            skPoint(sketch, "E22.16.1", {"position": v(6.24, -3.6) * mm});
            skArc(sketch, "E22.16.2", {"start": v(6.8, -3.66) * mm, "mid": v(6.26, -3.6) * mm, "end": v(5.72, -3.47) * mm});
            skArc(sketch, "E22.16.3", {"start": v(7.15, -3.11) * mm, "mid": v(7.04, -3.36) * mm, "end": v(6.92, -3.6) * mm});
            skPoint(sketch, "E22.16.4", {"position": v(6.89, -3.66) * mm});
            skPoint(sketch, "E22.16.5", {"position": v(6.22, -2.2) * mm});
            skArc(sketch, "E22.16.6", {"start": v(7.13, -2.99) * mm, "mid": v(6.74, -2.6) * mm, "end": v(6.3, -2.26) * mm});
            skPoint(sketch, "E22.16.7", {"position": v(7.18, -3.04) * mm});
            skArc(sketch, "E22.16.8", {"start": v(5.72, -3.47) * mm, "mid": v(5.64, -3.48) * mm, "end": v(5.58, -3.53) * mm});
            skArc(sketch, "E22.16.9", {"start": v(7.15, -3.11) * mm, "mid": v(7.16, -3.05) * mm, "end": v(7.13, -2.99) * mm});
            skArc(sketch, "E22.16.10", {"start": v(6.25, -2.12) * mm, "mid": v(6.25, -2.2) * mm, "end": v(6.3, -2.26) * mm});
            skArc(sketch, "E22.16.11", {"start": v(6.8, -3.66) * mm, "mid": v(6.87, -3.65) * mm, "end": v(6.92, -3.6) * mm});
            skPoint(sketch, "E22.17.0", {"position": v(6.33, -1.87) * mm});
            skPoint(sketch, "E22.17.1", {"position": v(6.95, -1.86) * mm});
            skArc(sketch, "E22.17.2", {"start": v(7.53, -1.77) * mm, "mid": v(6.98, -1.86) * mm, "end": v(6.42, -1.88) * mm});
            skArc(sketch, "E22.17.3", {"start": v(7.71, -1.16) * mm, "mid": v(7.67, -1.42) * mm, "end": v(7.62, -1.68) * mm});
            skPoint(sketch, "E22.17.4", {"position": v(7.6, -1.76) * mm});
            skPoint(sketch, "E22.17.5", {"position": v(6.58, -0.52) * mm});
            skArc(sketch, "E22.17.6", {"start": v(7.66, -1.04) * mm, "mid": v(7.18, -0.76) * mm, "end": v(6.67, -0.55) * mm});
            skPoint(sketch, "E22.17.7", {"position": v(7.72, -1.08) * mm});
            skArc(sketch, "E22.17.8", {"start": v(6.42, -1.88) * mm, "mid": v(6.35, -1.9) * mm, "end": v(6.3, -1.96) * mm});
            skArc(sketch, "E22.17.9", {"start": v(7.71, -1.16) * mm, "mid": v(7.7, -1.1) * mm, "end": v(7.66, -1.04) * mm});
            skArc(sketch, "E22.17.10", {"start": v(6.59, -0.43) * mm, "mid": v(6.6, -0.5) * mm, "end": v(6.67, -0.55) * mm});
            skArc(sketch, "E22.17.11", {"start": v(7.53, -1.77) * mm, "mid": v(7.58, -1.74) * mm, "end": v(7.62, -1.68) * mm});
            skPoint(sketch, "E22.18.0", {"position": v(6.6, -0.17) * mm});
            skPoint(sketch, "E22.18.1", {"position": v(7.2, 0) * mm});
            skArc(sketch, "E22.18.2", {"start": v(7.73, 0.23) * mm, "mid": v(7.22, 0) * mm, "end": v(6.69, -0.15) * mm});
            skArc(sketch, "E22.18.3", {"start": v(7.75, 0.88) * mm, "mid": v(7.78, 0.61) * mm, "end": v(7.8, 0.34) * mm});
            skPoint(sketch, "E22.18.4", {"position": v(7.8, 0.27) * mm});
            skPoint(sketch, "E22.18.5", {"position": v(6.49, 1.2) * mm});
            skArc(sketch, "E22.18.6", {"start": v(7.67, 0.98) * mm, "mid": v(7.13, 1.12) * mm, "end": v(6.58, 1.2) * mm});
            skPoint(sketch, "E22.18.7", {"position": v(7.74, 0.95) * mm});
            skArc(sketch, "E22.18.8", {"start": v(6.69, -0.15) * mm, "mid": v(6.62, -0.2) * mm, "end": v(6.6, -0.26) * mm});
            skArc(sketch, "E22.18.9", {"start": v(7.75, 0.88) * mm, "mid": v(7.72, 0.94) * mm, "end": v(7.67, 0.98) * mm});
            skArc(sketch, "E22.18.10", {"start": v(6.47, 1.3) * mm, "mid": v(6.51, 1.23) * mm, "end": v(6.58, 1.2) * mm});
            skArc(sketch, "E22.18.11", {"start": v(7.73, 0.23) * mm, "mid": v(7.78, 0.28) * mm, "end": v(7.8, 0.34) * mm});
            skPoint(sketch, "E22.19.0", {"position": v(6.42, 1.54) * mm});
            skPoint(sketch, "E22.19.1", {"position": v(6.95, 1.86) * mm});
            skArc(sketch, "E22.19.2", {"start": v(7.4, 2.23) * mm, "mid": v(6.97, 1.88) * mm, "end": v(6.5, 1.58) * mm});
            skArc(sketch, "E22.19.3", {"start": v(7.26, 2.85) * mm, "mid": v(7.35, 2.6) * mm, "end": v(7.44, 2.35) * mm});
            skPoint(sketch, "E22.19.4", {"position": v(7.46, 2.28) * mm});
            skPoint(sketch, "E22.19.5", {"position": v(5.96, 2.84) * mm});
            skArc(sketch, "E22.19.6", {"start": v(7.15, 2.93) * mm, "mid": v(6.6, 2.93) * mm, "end": v(6.05, 2.86) * mm});
            skPoint(sketch, "E22.19.7", {"position": v(7.23, 2.92) * mm});
            skArc(sketch, "E22.19.8", {"start": v(6.5, 1.58) * mm, "mid": v(6.45, 1.53) * mm, "end": v(6.44, 1.45) * mm});
            skArc(sketch, "E22.19.9", {"start": v(7.26, 2.85) * mm, "mid": v(7.22, 2.9) * mm, "end": v(7.15, 2.93) * mm});
            skArc(sketch, "E22.19.10", {"start": v(5.92, 2.92) * mm, "mid": v(5.97, 2.87) * mm, "end": v(6.05, 2.86) * mm});
            skArc(sketch, "E22.19.11", {"start": v(7.4, 2.23) * mm, "mid": v(7.44, 2.28) * mm, "end": v(7.44, 2.35) * mm});
            skPoint(sketch, "E23.0.20.0", {"position": v(5.8, 3.15) * mm});
            skPoint(sketch, "E23.1.20.0", {"position": v(6.24, 3.6) * mm});
            skArc(sketch, "E23.2.20.0", {"start": v(6.58, 4.07) * mm, "mid": v(6.25, 3.62) * mm, "end": v(5.87, 3.21) * mm});
            skArc(sketch, "E23.6.20.0", {"start": v(6.27, 4.64) * mm, "mid": v(6.43, 4.42) * mm, "end": v(6.58, 4.2) * mm});
            skPoint(sketch, "E23.10.20.0", {"position": v(6.62, 4.13) * mm});
            skPoint(sketch, "E23.11.20.0", {"position": v(5.02, 4.28) * mm});
            skArc(sketch, "E23.12.20.0", {"start": v(6.15, 4.68) * mm, "mid": v(5.62, 4.54) * mm, "end": v(5.1, 4.33) * mm});
            skPoint(sketch, "E23.16.20.0", {"position": v(6.23, 4.7) * mm});
            skArc(sketch, "E23.17.20.0", {"start": v(5.87, 3.21) * mm, "mid": v(5.83, 3.15) * mm, "end": v(5.84, 3.07) * mm});
            skArc(sketch, "E23.21.20.0", {"start": v(6.27, 4.64) * mm, "mid": v(6.22, 4.68) * mm, "end": v(6.15, 4.68) * mm});
            skArc(sketch, "E23.25.20.0", {"start": v(4.96, 4.35) * mm, "mid": v(5.03, 4.32) * mm, "end": v(5.1, 4.33) * mm});
            skArc(sketch, "E23.29.20.0", {"start": v(6.58, 4.07) * mm, "mid": v(6.6, 4.13) * mm, "end": v(6.58, 4.2) * mm});
            skPoint(sketch, "E23.0.21.0", {"position": v(4.79, 4.54) * mm});
            skPoint(sketch, "E23.1.21.0", {"position": v(5.1, 5.1) * mm});
            skArc(sketch, "E23.2.21.0", {"start": v(5.3, 5.63) * mm, "mid": v(5.1, 5.11) * mm, "end": v(4.84, 4.62) * mm});
            skArc(sketch, "E23.6.21.0", {"start": v(4.86, 6.1) * mm, "mid": v(5.07, 5.93) * mm, "end": v(5.27, 5.75) * mm});
            skPoint(sketch, "E23.10.21.0", {"position": v(5.32, 5.7) * mm});
            skPoint(sketch, "E23.11.21.0", {"position": v(3.74, 5.44) * mm});
            skArc(sketch, "E23.12.21.0", {"start": v(4.73, 6.12) * mm, "mid": v(4.25, 5.84) * mm, "end": v(3.8, 5.5) * mm});
            skPoint(sketch, "E23.16.21.0", {"position": v(4.8, 6.15) * mm});
            skArc(sketch, "E23.17.21.0", {"start": v(4.84, 4.62) * mm, "mid": v(4.82, 4.55) * mm, "end": v(4.85, 4.48) * mm});
            skArc(sketch, "E23.21.21.0", {"start": v(4.86, 6.1) * mm, "mid": v(4.8, 6.13) * mm, "end": v(4.73, 6.12) * mm});
            skArc(sketch, "E23.25.21.0", {"start": v(3.66, 5.5) * mm, "mid": v(3.74, 5.47) * mm, "end": v(3.8, 5.5) * mm});
            skArc(sketch, "E23.29.21.0", {"start": v(5.3, 5.63) * mm, "mid": v(5.3, 5.7) * mm, "end": v(5.27, 5.75) * mm});
            skPoint(sketch, "E23.0.22.0", {"position": v(3.45, 5.63) * mm});
            skPoint(sketch, "E23.1.22.0", {"position": v(3.6, 6.24) * mm});
            skArc(sketch, "E23.2.22.0", {"start": v(3.66, 6.8) * mm, "mid": v(3.6, 6.26) * mm, "end": v(3.47, 5.72) * mm});
            skArc(sketch, "E23.6.22.0", {"start": v(3.11, 7.15) * mm, "mid": v(3.36, 7.04) * mm, "end": v(3.6, 6.92) * mm});
            skPoint(sketch, "E23.10.22.0", {"position": v(3.66, 6.89) * mm});
            skPoint(sketch, "E23.11.22.0", {"position": v(2.2, 6.22) * mm});
            skArc(sketch, "E23.12.22.0", {"start": v(2.99, 7.13) * mm, "mid": v(2.6, 6.74) * mm, "end": v(2.26, 6.3) * mm});
            skPoint(sketch, "E23.16.22.0", {"position": v(3.04, 7.18) * mm});
            skArc(sketch, "E23.17.22.0", {"start": v(3.47, 5.72) * mm, "mid": v(3.48, 5.64) * mm, "end": v(3.53, 5.58) * mm});
            skArc(sketch, "E23.21.22.0", {"start": v(3.11, 7.15) * mm, "mid": v(3.05, 7.16) * mm, "end": v(2.99, 7.13) * mm});
            skArc(sketch, "E23.25.22.0", {"start": v(2.12, 6.25) * mm, "mid": v(2.2, 6.25) * mm, "end": v(2.26, 6.3) * mm});
            skArc(sketch, "E23.29.22.0", {"start": v(3.66, 6.8) * mm, "mid": v(3.65, 6.87) * mm, "end": v(3.6, 6.92) * mm});
            skPoint(sketch, "E23.0.23.0", {"position": v(1.87, 6.33) * mm});
            skPoint(sketch, "E23.1.23.0", {"position": v(1.86, 6.95) * mm});
            skArc(sketch, "E23.2.23.0", {"start": v(1.77, 7.53) * mm, "mid": v(1.86, 6.98) * mm, "end": v(1.88, 6.42) * mm});
            skArc(sketch, "E23.6.23.0", {"start": v(1.16, 7.71) * mm, "mid": v(1.42, 7.67) * mm, "end": v(1.68, 7.62) * mm});
            skPoint(sketch, "E23.10.23.0", {"position": v(1.76, 7.6) * mm});
            skPoint(sketch, "E23.11.23.0", {"position": v(0.52, 6.58) * mm});
            skArc(sketch, "E23.12.23.0", {"start": v(1.04, 7.66) * mm, "mid": v(0.76, 7.18) * mm, "end": v(0.55, 6.67) * mm});
            skPoint(sketch, "E23.16.23.0", {"position": v(1.08, 7.72) * mm});
            skArc(sketch, "E23.17.23.0", {"start": v(1.88, 6.42) * mm, "mid": v(1.9, 6.35) * mm, "end": v(1.96, 6.3) * mm});
            skArc(sketch, "E23.21.23.0", {"start": v(1.16, 7.71) * mm, "mid": v(1.1, 7.7) * mm, "end": v(1.04, 7.66) * mm});
            skArc(sketch, "E23.25.23.0", {"start": v(0.43, 6.59) * mm, "mid": v(0.5, 6.6) * mm, "end": v(0.55, 6.67) * mm});
            skArc(sketch, "E23.29.23.0", {"start": v(1.77, 7.53) * mm, "mid": v(1.74, 7.58) * mm, "end": v(1.68, 7.62) * mm});
            skSolve(sketch);
        }
        {
            var Q0;
            Q0=qSketchRegion(id+"F0",true);
            extrude(context, id + "F1", {"entities" : qUnion([Q0]), "depth" : 4.2 * mm});
        }
        {
            var Q0;
            Q0=qCreatedBy(makeId("Front.planeOp"),FACE);
            var sketch = newSketch(context, id + "F2", { "sketchPlane" : qUnion([Q0])});
            skCircle(sketch, "E24", {"center": v(0, 0) * mm, "radius": 16.5 * mm});
            skSolve(sketch);
        }
        {
            var Q0;
            Q0=qSketchRegion(id+"F2",true);
            extrude(context, id + "F3", {"entities" : qUnion([Q0]), "operationType" : NewBodyOperationType.ADD, "oppositeDirection" : true, "depth" : 2.5 * mm});
        }
        {
            var Q0;
            Q0=makeQuery(id+"F1.opExtrude","CAP_FACE",FACE,{"disambiguationData":[OSD([sQuery(id+"F0.wireOp",EDGE,"E13"),sQuery(id+"F0.wireOp",EDGE,"E14.MirrorCS"),sQuery(id+"F0.wireOp",EDGE,"E15"),sQuery(id+"F0.wireOp",EDGE,"E16"),sQuery(id+"F0.wireOp",EDGE,"E17.filletArc"),sQuery(id+"F0.wireOp",EDGE,"E18.filletArc"),sQuery(id+"F0.wireOp",EDGE,"E19.filletArc"),sQuery(id+"F0.wireOp",EDGE,"E20.filletArc"),sQuery(id+"F0.wireOp",EDGE,"E22.1.2"),sQuery(id+"F0.wireOp",EDGE,"E22.1.3"),sQuery(id+"F0.wireOp",EDGE,"E22.1.6"),sQuery(id+"F0.wireOp",EDGE,"E22.1.8"),sQuery(id+"F0.wireOp",EDGE,"E22.1.9"),sQuery(id+"F0.wireOp",EDGE,"E22.1.10"),sQuery(id+"F0.wireOp",EDGE,"E22.1.11"),sQuery(id+"F0.wireOp",EDGE,"E22.2.2"),sQuery(id+"F0.wireOp",EDGE,"E22.2.3"),sQuery(id+"F0.wireOp",EDGE,"E22.2.6"),sQuery(id+"F0.wireOp",EDGE,"E22.2.8"),sQuery(id+"F0.wireOp",EDGE,"E22.2.9"),sQuery(id+"F0.wireOp",EDGE,"E22.2.10"),sQuery(id+"F0.wireOp",EDGE,"E22.2.11"),sQuery(id+"F0.wireOp",EDGE,"E22.3.2"),sQuery(id+"F0.wireOp",EDGE,"E22.3.3"),sQuery(id+"F0.wireOp",EDGE,"E22.3.6"),sQuery(id+"F0.wireOp",EDGE,"E22.3.8"),sQuery(id+"F0.wireOp",EDGE,"E22.3.9"),sQuery(id+"F0.wireOp",EDGE,"E22.3.10"),sQuery(id+"F0.wireOp",EDGE,"E22.3.11"),sQuery(id+"F0.wireOp",EDGE,"E22.4.2"),sQuery(id+"F0.wireOp",EDGE,"E22.4.3"),sQuery(id+"F0.wireOp",EDGE,"E22.4.6"),sQuery(id+"F0.wireOp",EDGE,"E22.4.8"),sQuery(id+"F0.wireOp",EDGE,"E22.4.9"),sQuery(id+"F0.wireOp",EDGE,"E22.4.10"),sQuery(id+"F0.wireOp",EDGE,"E22.4.11"),sQuery(id+"F0.wireOp",EDGE,"E22.5.2"),sQuery(id+"F0.wireOp",EDGE,"E22.5.3"),sQuery(id+"F0.wireOp",EDGE,"E22.5.6"),sQuery(id+"F0.wireOp",EDGE,"E22.5.8"),sQuery(id+"F0.wireOp",EDGE,"E22.5.9"),sQuery(id+"F0.wireOp",EDGE,"E22.5.10"),sQuery(id+"F0.wireOp",EDGE,"E22.5.11"),sQuery(id+"F0.wireOp",EDGE,"E22.6.2"),sQuery(id+"F0.wireOp",EDGE,"E22.6.3"),sQuery(id+"F0.wireOp",EDGE,"E22.6.6"),sQuery(id+"F0.wireOp",EDGE,"E22.6.8"),sQuery(id+"F0.wireOp",EDGE,"E22.6.9"),sQuery(id+"F0.wireOp",EDGE,"E22.6.10"),sQuery(id+"F0.wireOp",EDGE,"E22.6.11"),sQuery(id+"F0.wireOp",EDGE,"E22.7.2"),sQuery(id+"F0.wireOp",EDGE,"E22.7.3"),sQuery(id+"F0.wireOp",EDGE,"E22.7.6"),sQuery(id+"F0.wireOp",EDGE,"E22.7.8"),sQuery(id+"F0.wireOp",EDGE,"E22.7.9"),sQuery(id+"F0.wireOp",EDGE,"E22.7.10"),sQuery(id+"F0.wireOp",EDGE,"E22.7.11"),sQuery(id+"F0.wireOp",EDGE,"E22.8.2"),sQuery(id+"F0.wireOp",EDGE,"E22.8.3"),sQuery(id+"F0.wireOp",EDGE,"E22.8.6"),sQuery(id+"F0.wireOp",EDGE,"E22.8.8"),sQuery(id+"F0.wireOp",EDGE,"E22.8.9"),sQuery(id+"F0.wireOp",EDGE,"E22.8.10"),sQuery(id+"F0.wireOp",EDGE,"E22.8.11"),sQuery(id+"F0.wireOp",EDGE,"E22.9.2"),sQuery(id+"F0.wireOp",EDGE,"E22.9.3"),sQuery(id+"F0.wireOp",EDGE,"E22.9.6"),sQuery(id+"F0.wireOp",EDGE,"E22.9.8"),sQuery(id+"F0.wireOp",EDGE,"E22.9.9"),sQuery(id+"F0.wireOp",EDGE,"E22.9.10"),sQuery(id+"F0.wireOp",EDGE,"E22.9.11"),sQuery(id+"F0.wireOp",EDGE,"E22.10.2"),sQuery(id+"F0.wireOp",EDGE,"E22.10.3"),sQuery(id+"F0.wireOp",EDGE,"E22.10.6"),sQuery(id+"F0.wireOp",EDGE,"E22.10.8"),sQuery(id+"F0.wireOp",EDGE,"E22.10.9"),sQuery(id+"F0.wireOp",EDGE,"E22.10.10"),sQuery(id+"F0.wireOp",EDGE,"E22.10.11"),sQuery(id+"F0.wireOp",EDGE,"E22.11.2"),sQuery(id+"F0.wireOp",EDGE,"E22.11.3"),sQuery(id+"F0.wireOp",EDGE,"E22.11.6"),sQuery(id+"F0.wireOp",EDGE,"E22.11.8"),sQuery(id+"F0.wireOp",EDGE,"E22.11.9"),sQuery(id+"F0.wireOp",EDGE,"E22.11.10"),sQuery(id+"F0.wireOp",EDGE,"E22.11.11"),sQuery(id+"F0.wireOp",EDGE,"E22.12.2"),sQuery(id+"F0.wireOp",EDGE,"E22.12.3"),sQuery(id+"F0.wireOp",EDGE,"E22.12.6"),sQuery(id+"F0.wireOp",EDGE,"E22.12.8"),sQuery(id+"F0.wireOp",EDGE,"E22.12.9"),sQuery(id+"F0.wireOp",EDGE,"E22.12.10"),sQuery(id+"F0.wireOp",EDGE,"E22.12.11"),sQuery(id+"F0.wireOp",EDGE,"E22.13.2"),sQuery(id+"F0.wireOp",EDGE,"E22.13.3"),sQuery(id+"F0.wireOp",EDGE,"E22.13.6"),sQuery(id+"F0.wireOp",EDGE,"E22.13.8"),sQuery(id+"F0.wireOp",EDGE,"E22.13.9"),sQuery(id+"F0.wireOp",EDGE,"E22.13.10"),sQuery(id+"F0.wireOp",EDGE,"E22.13.11"),sQuery(id+"F0.wireOp",EDGE,"E22.14.2"),sQuery(id+"F0.wireOp",EDGE,"E22.14.3"),sQuery(id+"F0.wireOp",EDGE,"E22.14.6"),sQuery(id+"F0.wireOp",EDGE,"E22.14.8"),sQuery(id+"F0.wireOp",EDGE,"E22.14.9"),sQuery(id+"F0.wireOp",EDGE,"E22.14.10"),sQuery(id+"F0.wireOp",EDGE,"E22.14.11"),sQuery(id+"F0.wireOp",EDGE,"E22.15.2"),sQuery(id+"F0.wireOp",EDGE,"E22.15.3"),sQuery(id+"F0.wireOp",EDGE,"E22.15.6"),sQuery(id+"F0.wireOp",EDGE,"E22.15.8"),sQuery(id+"F0.wireOp",EDGE,"E22.15.9"),sQuery(id+"F0.wireOp",EDGE,"E22.15.10"),sQuery(id+"F0.wireOp",EDGE,"E22.15.11"),sQuery(id+"F0.wireOp",EDGE,"E22.16.2"),sQuery(id+"F0.wireOp",EDGE,"E22.16.3"),sQuery(id+"F0.wireOp",EDGE,"E22.16.6"),sQuery(id+"F0.wireOp",EDGE,"E22.16.8"),sQuery(id+"F0.wireOp",EDGE,"E22.16.9"),sQuery(id+"F0.wireOp",EDGE,"E22.16.10"),sQuery(id+"F0.wireOp",EDGE,"E22.16.11"),sQuery(id+"F0.wireOp",EDGE,"E22.17.2"),sQuery(id+"F0.wireOp",EDGE,"E22.17.3"),sQuery(id+"F0.wireOp",EDGE,"E22.17.6"),sQuery(id+"F0.wireOp",EDGE,"E22.17.8"),sQuery(id+"F0.wireOp",EDGE,"E22.17.9"),sQuery(id+"F0.wireOp",EDGE,"E22.17.10"),sQuery(id+"F0.wireOp",EDGE,"E22.17.11"),sQuery(id+"F0.wireOp",EDGE,"E22.18.2"),sQuery(id+"F0.wireOp",EDGE,"E22.18.3"),sQuery(id+"F0.wireOp",EDGE,"E22.18.6"),sQuery(id+"F0.wireOp",EDGE,"E22.18.8"),sQuery(id+"F0.wireOp",EDGE,"E22.18.9"),sQuery(id+"F0.wireOp",EDGE,"E22.18.10"),sQuery(id+"F0.wireOp",EDGE,"E22.18.11"),sQuery(id+"F0.wireOp",EDGE,"E22.19.2"),sQuery(id+"F0.wireOp",EDGE,"E22.19.3"),sQuery(id+"F0.wireOp",EDGE,"E22.19.6"),sQuery(id+"F0.wireOp",EDGE,"E22.19.8"),sQuery(id+"F0.wireOp",EDGE,"E22.19.9"),sQuery(id+"F0.wireOp",EDGE,"E22.19.10"),sQuery(id+"F0.wireOp",EDGE,"E22.19.11")])],"isStart":false});
            var sketch = newSketch(context, id + "F4", { "sketchPlane" : qUnion([Q0])});
            skCircle(sketch, "E25", {"center": v(0, 0) * mm, "radius": 1.25 * mm});
            skSolve(sketch);
        }
        {
            var Q0;
            Q0=qSketchRegion(id+"F4",true);
            extrude(context, id + "F5", {"entities" : qUnion([Q0]), "operationType" : NewBodyOperationType.REMOVE, "oppositeDirection" : true, "depth" : 25 * mm});
        }
        {
            var Q0;
            Q0=makeQuery(id+"F3.opExtrude","CAP_FACE",FACE,{"disambiguationData":[OSD([sQuery(id+"F2.wireOp",EDGE,"E24")])],"isStart":false});
            var sketch = newSketch(context, id + "F6", { "sketchPlane" : qUnion([Q0])});
            skLineSegment(sketch, "E26", {"start": v(0, 0) * mm, "end": v(0, 16.5) * mm, "construction": true});
            skCircle(sketch, "E27", {"center": v(0, 13) * mm, "radius": 1 * mm});
            skCircle(sketch, "E28.1.0", {"center": v(-11.26, -6.5) * mm, "radius": 1 * mm});
            skCircle(sketch, "E28.2.0", {"center": v(11.26, -6.5) * mm, "radius": 1 * mm});
            skPoint(sketch, "E28.center", {"position": v(0, 0) * mm});
            skSolve(sketch);
        }
        {
            var Q0;
            Q0=qSketchRegion(id+"F6",true);
            extrude(context, id + "F7", {"entities" : qUnion([Q0]), "operationType" : NewBodyOperationType.ADD, "depth" : 3.8 * mm});
        }
    });
